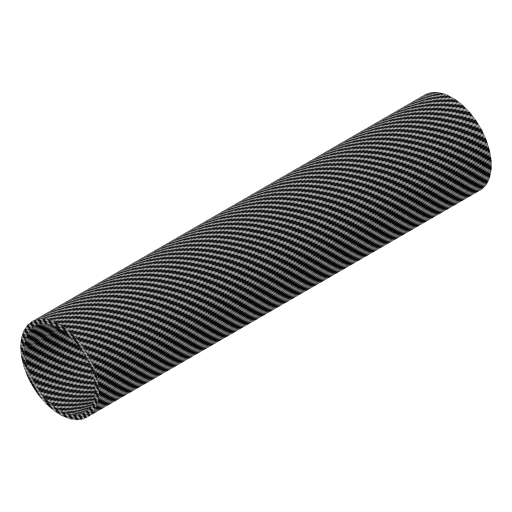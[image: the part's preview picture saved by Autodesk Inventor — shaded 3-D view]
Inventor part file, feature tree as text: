
AUTODESK INVENTOR PART (.ipt)
format: ipt  version: 2023.2 (Build 272271000, 271)  size: 205,312 bytes
history: native  units: mm
features: other x1, extrude x1, sketch x1
ambient origin geometry x8: Origin, YZ Plane, XZ Plane, XY Plane, X Axis, Y Axis, Z Axis, Center Point
bodies: Body1 (feature_tree)
feature tree (3):
  other  "솔리드1"
  extrude  "돌출1"  Depth=40.0mm
  sketch  "스케치1"
